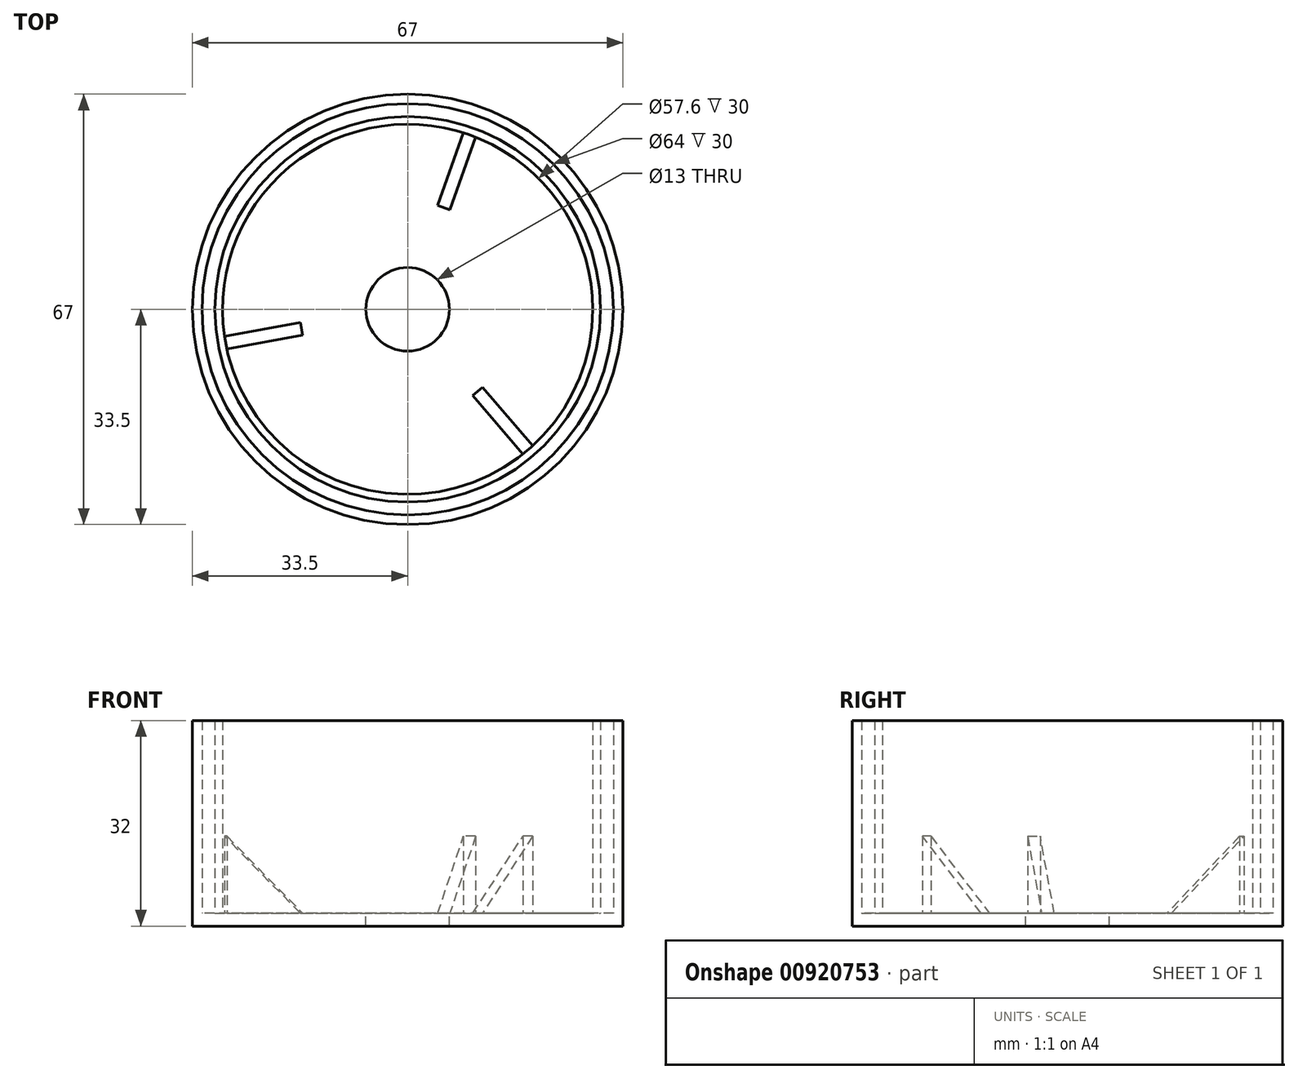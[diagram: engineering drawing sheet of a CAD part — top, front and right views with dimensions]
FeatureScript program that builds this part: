
annotation { "Feature Type Name" : "Feature", "Feature Type Description" : "" }
export const myFeature = defineFeature(function(context is Context, id is Id, definition is map)
    precondition{}
    {
        {
            var Q0;
            Q0=qCreatedBy(makeId("Top.planeOp"),FACE);
            var sketch = newSketch(context, id + "F0", { "sketchPlane" : qUnion([Q0])});
            skCircle(sketch, "E0", {"center": v(0, 0) * mm, "radius": 30 * mm});
            skCircle(sketch, "E1", {"center": v(0, 0) * mm, "radius": 28.8 * mm});
            skCircle(sketch, "E2", {"center": v(0, 0) * mm, "radius": 32 * mm});
            skCircle(sketch, "E3", {"center": v(0, 0) * mm, "radius": 33.5 * mm});
            skSolve(sketch);
        }
        {
            var Q0;
            Q0 = qSketchRegion(id + "F0", true);
            var Q1;
            Q1=makeQuery(id+"F0.imprint","IMPRINT",FACE,{"disambiguationData":[TD([[makeQuery(id+"F0.imprint","IMPRINT",EDGE,{"derivedFrom":sQuery(id+"F0.wireOp",EDGE,"E0")}),1.0]])]});
            extrude(context, id + "F1", {"entities" : qUnion([Q0, Q1]), "depth" : 30 * mm, "offsetDistance" : 25 * mm});
        }
        {
            var Q0;
            Q0=makeQuery(id+"F1.opExtrude","CAP_FACE",FACE,{"disambiguationData":[OSD([sQuery(id+"F0.wireOp",EDGE,"E2"),sQuery(id+"F0.wireOp",EDGE,"E3")])],"isStart":true});
            var sketch = newSketch(context, id + "F2", { "sketchPlane" : qUnion([Q0])});
            skCircle(sketch, "E4.0", {"center": v(0, 0) * mm, "radius": 33.5 * mm});
            skSolve(sketch);
        }
        {
            var Q0;
            Q0 = qSketchRegion(id + "F2", true);
            extrude(context, id + "F3", {"entities" : qUnion([Q0]), "depth" : 2 * mm, "offsetDistance" : 25 * mm});
        }
        {
            var Q0;
            Q0=makeQuery(id+"F3.opExtrude","CAP_FACE",FACE,{"disambiguationData":[OSD([sQuery(id+"F2.wireOp",EDGE,"E4.0"),sQuery(id+"F2.wireOp",EDGE,"ya3XJKNe-zwGp-OSvx-wKJr-Qpu3Fzca8BsL")])],"isStart":true});
            var sketch = newSketch(context, id + "F4", { "sketchPlane" : qUnion([Q0])});
            skCircle(sketch, "E5.0", {"center": v(0, 0) * mm, "radius": 28.8 * mm});
            skCircle(sketch, "E6.cCircle", {"center": v(0, 0) * mm, "radius": 28.8 * mm, "construction": true});
            skLineSegment(sketch, "E6.0", {"start": v(9.63, 27.14) * mm, "end": v(18.7, -21.91) * mm});
            skLineSegment(sketch, "E6.1", {"start": v(18.7, -21.91) * mm, "end": v(-28.32, -5.23) * mm});
            skLineSegment(sketch, "E6.2", {"start": v(-28.32, -5.23) * mm, "end": v(9.63, 27.14) * mm});
            skLineSegment(sketch, "E7", {"start": v(0, 0) * mm, "end": v(9.63, 27.14) * mm});
            skLineSegment(sketch, "E8", {"start": v(18.7, -21.91) * mm, "end": v(0, 0) * mm});
            skLineSegment(sketch, "E9", {"start": v(0, 0) * mm, "end": v(-28.32, -5.23) * mm});
            skLineSegment(sketch, "E10", {"start": v(5.62, 15.83) * mm, "end": v(6.56, 15.5) * mm});
            skLineSegment(sketch, "E11", {"start": v(6.56, 15.5) * mm, "end": v(10.57, 26.8) * mm});
            skLineSegment(sketch, "E12", {"start": v(5.62, 15.83) * mm, "end": v(4.68, 16.17) * mm});
            skLineSegment(sketch, "E13", {"start": v(4.68, 16.17) * mm, "end": v(8.68, 27.46) * mm});
            skLineSegment(sketch, "E14", {"start": v(-16.52, -3.03) * mm, "end": v(-16.7, -2.05) * mm});
            skLineSegment(sketch, "E15", {"start": v(-16.7, -2.05) * mm, "end": v(-28.49, -4.23) * mm});
            skLineSegment(sketch, "E16", {"start": v(-16.52, -3.03) * mm, "end": v(-16.34, -4.02) * mm});
            skLineSegment(sketch, "E17", {"start": v(-16.34, -4.02) * mm, "end": v(-28.13, -6.2) * mm});
            skLineSegment(sketch, "E18", {"start": v(10.9, -12.78) * mm, "end": v(11.66, -12.13) * mm});
            skLineSegment(sketch, "E19", {"start": v(10.9, -12.78) * mm, "end": v(10.14, -13.43) * mm});
            skLineSegment(sketch, "E20", {"start": v(11.66, -12.13) * mm, "end": v(19.44, -21.25) * mm});
            skLineSegment(sketch, "E21", {"start": v(10.14, -13.43) * mm, "end": v(17.92, -22.55) * mm});
            skSolve(sketch);
        }
        {
            var Q0;
            {var subQ1=sQuery(id+"F4.wireOp",EDGE,"E5.0");var subQ3=sQuery(id+"F4.wireOp",EDGE,"E11");var subQ4=makeQuery(id+"F4.imprint","INTERSECT",VERTEX,{"derivedFrom":[subQ1,subQ3]});Q0=makeQuery(id+"F4.imprint","IMPRINT",FACE,{"disambiguationData":[TD([[makeQuery(id+"F4.imprint","IMPRINT",EDGE,{"disambiguationData":[TD([[subQ4,1.0]])],"derivedFrom":subQ3}),1.0]])]});}
            var Q1;
            {var subQ1=sQuery(id+"F4.wireOp",EDGE,"E5.0");var subQ3=sQuery(id+"F4.wireOp",EDGE,"E13");var subQ4=makeQuery(id+"F4.imprint","INTERSECT",VERTEX,{"derivedFrom":[subQ1,subQ3]});Q1=makeQuery(id+"F4.imprint","IMPRINT",FACE,{"disambiguationData":[TD([[makeQuery(id+"F4.imprint","IMPRINT",EDGE,{"disambiguationData":[TD([[subQ4,1.0]])],"derivedFrom":subQ3}),-1.0]])]});}
            var Q2;
            {var subQ1=sQuery(id+"F4.wireOp",EDGE,"E5.0");var subQ3=sQuery(id+"F4.wireOp",EDGE,"E15");var subQ4=makeQuery(id+"F4.imprint","INTERSECT",VERTEX,{"derivedFrom":[subQ1,subQ3]});Q2=makeQuery(id+"F4.imprint","IMPRINT",FACE,{"disambiguationData":[TD([[makeQuery(id+"F4.imprint","IMPRINT",EDGE,{"disambiguationData":[TD([[subQ4,1.0]])],"derivedFrom":subQ3}),1.0]])]});}
            var Q3;
            {var subQ1=sQuery(id+"F4.wireOp",EDGE,"E5.0");var subQ3=sQuery(id+"F4.wireOp",EDGE,"E17");var subQ4=makeQuery(id+"F4.imprint","INTERSECT",VERTEX,{"derivedFrom":[subQ1,subQ3]});Q3=makeQuery(id+"F4.imprint","IMPRINT",FACE,{"disambiguationData":[TD([[makeQuery(id+"F4.imprint","IMPRINT",EDGE,{"disambiguationData":[TD([[subQ4,1.0]])],"derivedFrom":subQ3}),-1.0]])]});}
            var Q4;
            {var subQ1=sQuery(id+"F4.wireOp",EDGE,"E5.0");var subQ3=sQuery(id+"F4.wireOp",EDGE,"E21");var subQ4=makeQuery(id+"F4.imprint","INTERSECT",VERTEX,{"derivedFrom":[subQ1,subQ3]});Q4=makeQuery(id+"F4.imprint","IMPRINT",FACE,{"disambiguationData":[TD([[makeQuery(id+"F4.imprint","IMPRINT",EDGE,{"disambiguationData":[TD([[subQ4,1.0]])],"derivedFrom":subQ3}),1.0]])]});}
            var Q5;
            {var subQ1=sQuery(id+"F4.wireOp",EDGE,"E5.0");var subQ3=sQuery(id+"F4.wireOp",EDGE,"E20");var subQ4=makeQuery(id+"F4.imprint","INTERSECT",VERTEX,{"derivedFrom":[subQ1,subQ3]});Q5=makeQuery(id+"F4.imprint","IMPRINT",FACE,{"disambiguationData":[TD([[makeQuery(id+"F4.imprint","IMPRINT",EDGE,{"disambiguationData":[TD([[subQ4,1.0]])],"derivedFrom":subQ3}),-1.0]])]});}
            var Q6;
            {var subQ5=sQuery(id+"F4.wireOp",EDGE,"E10");Q6=makeQuery(id+"F4.imprint","IMPRINT",FACE,{"disambiguationData":[TD([[makeQuery(id+"F4.imprint","IMPRINT",EDGE,{"derivedFrom":subQ5}),1.0]])]});}
            var Q7;
            {var subQ5=sQuery(id+"F4.wireOp",EDGE,"E18");Q7=makeQuery(id+"F4.imprint","IMPRINT",FACE,{"disambiguationData":[TD([[makeQuery(id+"F4.imprint","IMPRINT",EDGE,{"derivedFrom":subQ5}),-1.0]])]});}
            var Q8;
            {var subQ5=sQuery(id+"F4.wireOp",EDGE,"E19");Q8=makeQuery(id+"F4.imprint","IMPRINT",FACE,{"disambiguationData":[TD([[makeQuery(id+"F4.imprint","IMPRINT",EDGE,{"derivedFrom":subQ5}),1.0]])]});}
            var Q9;
            {var subQ5=sQuery(id+"F4.wireOp",EDGE,"E16");Q9=makeQuery(id+"F4.imprint","IMPRINT",FACE,{"disambiguationData":[TD([[makeQuery(id+"F4.imprint","IMPRINT",EDGE,{"derivedFrom":subQ5}),-1.0]])]});}
            var Q10;
            {var subQ5=sQuery(id+"F4.wireOp",EDGE,"E14");Q10=makeQuery(id+"F4.imprint","IMPRINT",FACE,{"disambiguationData":[TD([[makeQuery(id+"F4.imprint","IMPRINT",EDGE,{"derivedFrom":subQ5}),1.0]])]});}
            var Q11;
            {var subQ5=sQuery(id+"F4.wireOp",EDGE,"E12");Q11=makeQuery(id+"F4.imprint","IMPRINT",FACE,{"disambiguationData":[TD([[makeQuery(id+"F4.imprint","IMPRINT",EDGE,{"derivedFrom":subQ5}),-1.0]])]});}
            extrude(context, id + "F5", {"entities" : qUnion([Q0, Q1, Q2, Q3, Q4, Q5, Q6, Q7, Q8, Q9, Q10, Q11]), "depth" : 12 * mm, "offsetDistance" : 25 * mm});
        }
        {
            var Q0;
            Q0=makeQuery(id+"F5.opExtrude","CAP_EDGE",EDGE,{"disambiguationData":[OSD([sQuery(id+"F4.wireOp",EDGE,"E14"),sQuery(id+"F4.wireOp",EDGE,"E16")])],"isStart":false});
            var Q1;
            Q1=makeQuery(id+"F5.opExtrude","CAP_EDGE",EDGE,{"disambiguationData":[OSD([sQuery(id+"F4.wireOp",EDGE,"E10"),sQuery(id+"F4.wireOp",EDGE,"E12")])],"isStart":false});
            var Q2;
            Q2=makeQuery(id+"F5.opExtrude","CAP_EDGE",EDGE,{"disambiguationData":[OSD([sQuery(id+"F4.wireOp",EDGE,"E18"),sQuery(id+"F4.wireOp",EDGE,"E19")])],"isStart":false});
            chamfer(context, id + "F6", {"entities" : qUnion([Q0, Q1, Q2]), "width" : 12 * mm, "tangentPropagation" : true});
        }
        {
            var Q0;
            Q0=makeQuery(id+"F5.opExtrude","SWEPT_BODY",BODY,{"disambiguationData":[OSD([sQuery(id+"F4.wireOp",EDGE,"E5.0"),sQuery(id+"F4.wireOp",EDGE,"E10"),sQuery(id+"F4.wireOp",EDGE,"E11"),sQuery(id+"F4.wireOp",EDGE,"E12"),sQuery(id+"F4.wireOp",EDGE,"E13")])]});
            var Q1;
            Q1=makeQuery(id+"F1.opExtrude","SWEPT_BODY",BODY,{"disambiguationData":[OSD([sQuery(id+"F0.wireOp",EDGE,"E0"),sQuery(id+"F0.wireOp",EDGE,"E1")])]});
            var Q2;
            Q2=makeQuery(id+"F1.opExtrude","SWEPT_BODY",BODY,{"disambiguationData":[OSD([sQuery(id+"F0.wireOp",EDGE,"E2"),sQuery(id+"F0.wireOp",EDGE,"E3")])]});
            var Q3;
            Q3=makeQuery(id+"F3.opExtrude","SWEPT_BODY",BODY,{"disambiguationData":[OSD([sQuery(id+"F2.wireOp",EDGE,"E4.0"),sQuery(id+"F2.wireOp",EDGE,"ya3XJKNe-zwGp-OSvx-wKJr-Qpu3Fzca8BsL")])]});
            var Q4;
            Q4=makeQuery(id+"F5.opExtrude","SWEPT_BODY",BODY,{"disambiguationData":[OSD([sQuery(id+"F4.wireOp",EDGE,"E5.0"),sQuery(id+"F4.wireOp",EDGE,"E14"),sQuery(id+"F4.wireOp",EDGE,"E15"),sQuery(id+"F4.wireOp",EDGE,"E16"),sQuery(id+"F4.wireOp",EDGE,"E17")])]});
            var Q5;
            Q5=makeQuery(id+"F5.opExtrude","SWEPT_BODY",BODY,{"disambiguationData":[OSD([sQuery(id+"F4.wireOp",EDGE,"E5.0"),sQuery(id+"F4.wireOp",EDGE,"E18"),sQuery(id+"F4.wireOp",EDGE,"E19"),sQuery(id+"F4.wireOp",EDGE,"E20"),sQuery(id+"F4.wireOp",EDGE,"E21")])]});
            booleanBodies(context, id + "F7", {"operationType" : BooleanOperationType.UNION, "tools" : qUnion([Q0, Q1, Q2, Q3, Q4, Q5])});
        }
        {
            var Q0;
            Q0=makeQuery(id+"F7.opBoolean","SPLIT",FACE,{"disambiguationData":[TD([makeQuery(id+"F1.opExtrude","SWEPT_FACE",FACE,{"disambiguationData":[OSD([sQuery(id+"F0.wireOp",EDGE,"E1")])]})])],"derivedFrom":makeQuery(id+"F3.opExtrude","CAP_FACE",FACE,{"disambiguationData":[OSD([sQuery(id+"F2.wireOp",EDGE,"E4.0")])],"isStart":true})});
            var sketch = newSketch(context, id + "F8", { "sketchPlane" : qUnion([Q0])});
            skCircle(sketch, "E22", {"center": v(0, 0) * mm, "radius": 6.5 * mm});
            skSolve(sketch);
        }
        {
            var Q0;
            Q0=makeQuery(id+"F8.imprint","IMPRINT",FACE,{"disambiguationData":[TD([[makeQuery(id+"F8.imprint","IMPRINT",EDGE,{"derivedFrom":sQuery(id+"F8.wireOp",EDGE,"E22")}),1.0]])]});
            extrude(context, id + "F9", {"entities" : qUnion([Q0]), "operationType" : NewBodyOperationType.REMOVE, "oppositeDirection" : true, "depth" : 25 * mm, "offsetDistance" : 25 * mm});
        }
    });
